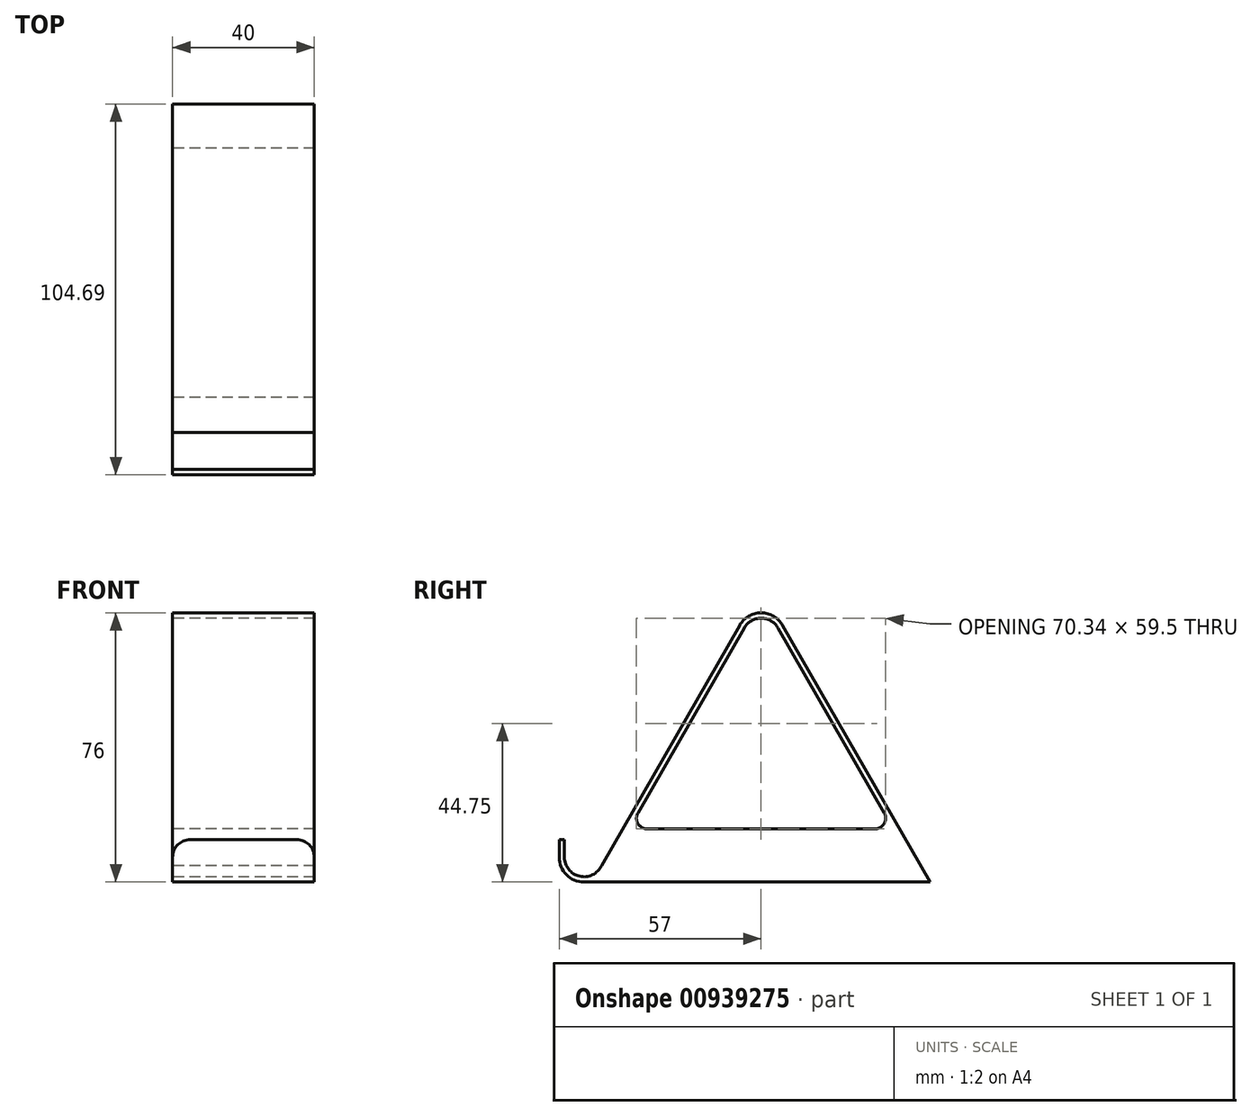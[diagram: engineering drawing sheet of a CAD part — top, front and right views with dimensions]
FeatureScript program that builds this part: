
annotation { "Feature Type Name" : "Feature", "Feature Type Description" : "" }
export const myFeature = defineFeature(function(context is Context, id is Id, definition is map)
    precondition{}
    {
        {
            var Q0;
            Q0=qCreatedBy(makeId("Right.planeOp"),FACE);
            var sketch = newSketch(context, id + "F0", { "sketchPlane" : qUnion([Q0])});
            skArc(sketch, "E0", {"start": v(-7, 0) * mm, "mid": v(-4.95, -4.95) * mm, "end": v(0, -7) * mm});
            skArc(sketch, "E1", {"start": v(54.77, 64.74) * mm, "mid": v(50, 67.5) * mm, "end": v(45.23, 64.74) * mm});
            skLineSegment(sketch, "E2", {"start": v(15.23, 12.5) * mm, "end": v(45.23, 64.74) * mm});
            skLineSegment(sketch, "E3", {"start": v(50, 62) * mm, "end": v(50, -50.79) * mm, "construction": true});
            skLineSegment(sketch, "E4.MirrorCS", {"start": v(84.77, 12.5) * mm, "end": v(54.77, 64.74) * mm});
            skLineSegment(sketch, "E5", {"start": v(0, -7) * mm, "end": v(114.86, -7) * mm, "construction": true});
            skLineSegment(sketch, "E6", {"start": v(-7, 0) * mm, "end": v(-7, 5) * mm});
            skLineSegment(sketch, "E7.0", {"start": v(-5.5, 0) * mm, "end": v(-5.5, 5) * mm});
            skLineSegment(sketch, "E7.1", {"start": v(97.7, -7) * mm, "end": v(56.07, 65.49) * mm});
            skArc(sketch, "E7.2", {"start": v(56.07, 65.49) * mm, "mid": v(50, 69) * mm, "end": v(43.93, 65.49) * mm});
            skLineSegment(sketch, "E7.3", {"start": v(4.96, -2.38) * mm, "end": v(43.93, 65.49) * mm});
            skArc(sketch, "E7.4", {"start": v(-5.5, 0) * mm, "mid": v(-1.22, -5.36) * mm, "end": v(4.96, -2.38) * mm});
            skLineSegment(sketch, "E8", {"start": v(-7, 5) * mm, "end": v(-5.5, 5) * mm});
            skLineSegment(sketch, "E9", {"start": v(0, -7) * mm, "end": v(97.7, -7) * mm});
            skLineSegment(sketch, "E10.trimOffspring", {"start": v(17.83, 8) * mm, "end": v(82.17, 8) * mm});
            skPoint(sketch, "E11.visualSharp", {"position": v(12.65, 8) * mm});
            skArc(sketch, "E11.filletArc", {"start": v(15.23, 12.5) * mm, "mid": v(15.23, 9.5) * mm, "end": v(17.83, 8) * mm});
            skPoint(sketch, "E12.visualSharp", {"position": v(87.35, 8) * mm});
            skArc(sketch, "E12.filletArc", {"start": v(82.17, 8) * mm, "mid": v(84.77, 9.5) * mm, "end": v(84.77, 12.5) * mm});
            skSolve(sketch);
        }
        {
            var Q0;
            Q0=makeQuery(id+"F0.imprint","IMPRINT",FACE,{"disambiguationData":[TD([[makeQuery(id+"F0.imprint","IMPRINT",EDGE,{"derivedFrom":sQuery(id+"F0.wireOp",EDGE,"E0")}),1.0]])]});
            extrude(context, id + "F1", {"entities" : qUnion([Q0]), "depth" : 40 * mm, "offsetDistance" : 25 * mm});
        }
        {
            var Q0;
            Q0=makeQuery(id+"F1.opExtrude","CAP_EDGE",EDGE,{"disambiguationData":[OSD([sQuery(id+"F0.wireOp",EDGE,"E8")])],"isStart":false});
            var Q1;
            Q1=makeQuery(id+"F1.opExtrude","CAP_EDGE",EDGE,{"disambiguationData":[OSD([sQuery(id+"F0.wireOp",EDGE,"E8")])],"isStart":true});
            fillet(context, id + "F2", {"entities" : qUnion([Q0, Q1]), "radius" : 5 * mm, "tangentPropagation" : true, "allowEdgeOverflow" : false});
        }
    });
